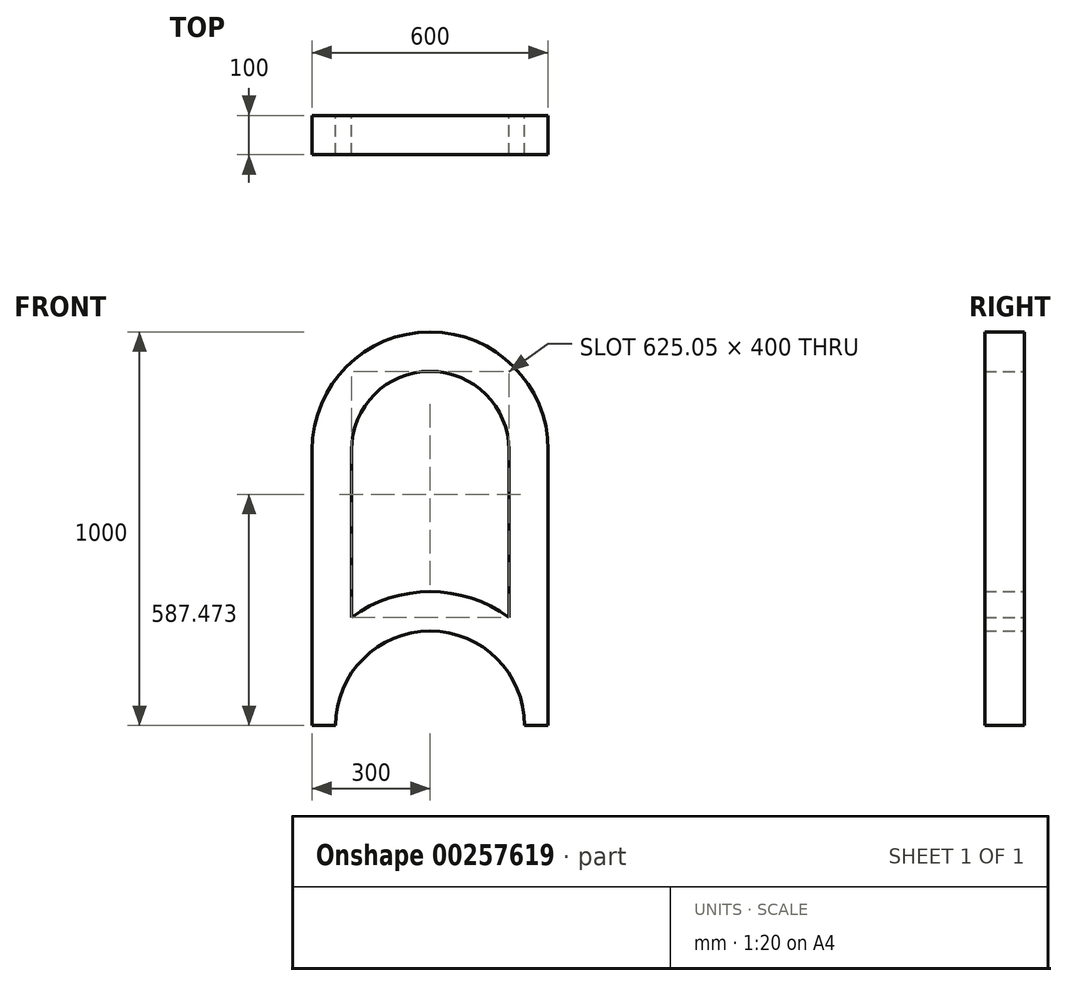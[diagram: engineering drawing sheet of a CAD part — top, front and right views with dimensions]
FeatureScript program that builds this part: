
annotation { "Feature Type Name" : "Feature", "Feature Type Description" : "" }
export const myFeature = defineFeature(function(context is Context, id is Id, definition is map)
    precondition{}
    {
        {
            var Q0;
            Q0=qCreatedBy(makeId("Front.planeOp"),FACE);
            var sketch = newSketch(context, id + "F0", { "sketchPlane" : qUnion([Q0])});
            skLineSegment(sketch, "E0", {"start": v(-60, -42.97) * mm, "end": v(0, -42.97) * mm});
            skLineSegment(sketch, "E1", {"start": v(540, -42.97) * mm, "end": v(480, -42.97) * mm});
            skArc(sketch, "E2", {"start": v(480, -42.97) * mm, "mid": v(240, 197.03) * mm, "end": v(0, -42.97) * mm});
            skArc(sketch, "E3", {"start": v(440, 231.98) * mm, "mid": v(240, 297.03) * mm, "end": v(40, 231.98) * mm});
            skLineSegment(sketch, "E4", {"start": v(-60, -42.97) * mm, "end": v(-60, 117.03) * mm});
            skLineSegment(sketch, "E5", {"start": v(540, -42.97) * mm, "end": v(540, 117.03) * mm});
            skArc(sketch, "E6", {"start": v(440, 657.03) * mm, "mid": v(240, 857.03) * mm, "end": v(40, 657.03) * mm});
            skArc(sketch, "E7", {"start": v(540, 657.03) * mm, "mid": v(240, 957.03) * mm, "end": v(-60, 657.03) * mm});
            skLineSegment(sketch, "E8", {"start": v(540, 117.03) * mm, "end": v(540, 657.03) * mm});
            skLineSegment(sketch, "E9", {"start": v(-60, 117.03) * mm, "end": v(-60, 657.03) * mm});
            skLineSegment(sketch, "E10", {"start": v(40, 657.03) * mm, "end": v(40, 231.98) * mm});
            skLineSegment(sketch, "E11", {"start": v(440, 657.03) * mm, "end": v(440, 231.98) * mm});
            skLineSegment(sketch, "E12.trimOffspring", {"start": v(480, -42.97) * mm, "end": v(540, -42.97) * mm});
            skPoint(sketch, "E13.end.orphan", {"position": v(240, 297.03) * mm});
            skSolve(sketch);
        }
        {
            var Q0;
            Q0=makeQuery(id+"F0.imprint","IMPRINT",FACE,{"disambiguationData":[TD([[makeQuery(id+"F0.imprint","IMPRINT",EDGE,{"derivedFrom":sQuery(id+"F0.wireOp",EDGE,"E0")}),1.0]])]});
            extrude(context, id + "F1", {"entities" : qUnion([Q0]), "depth" : 100 * mm});
        }
    });
